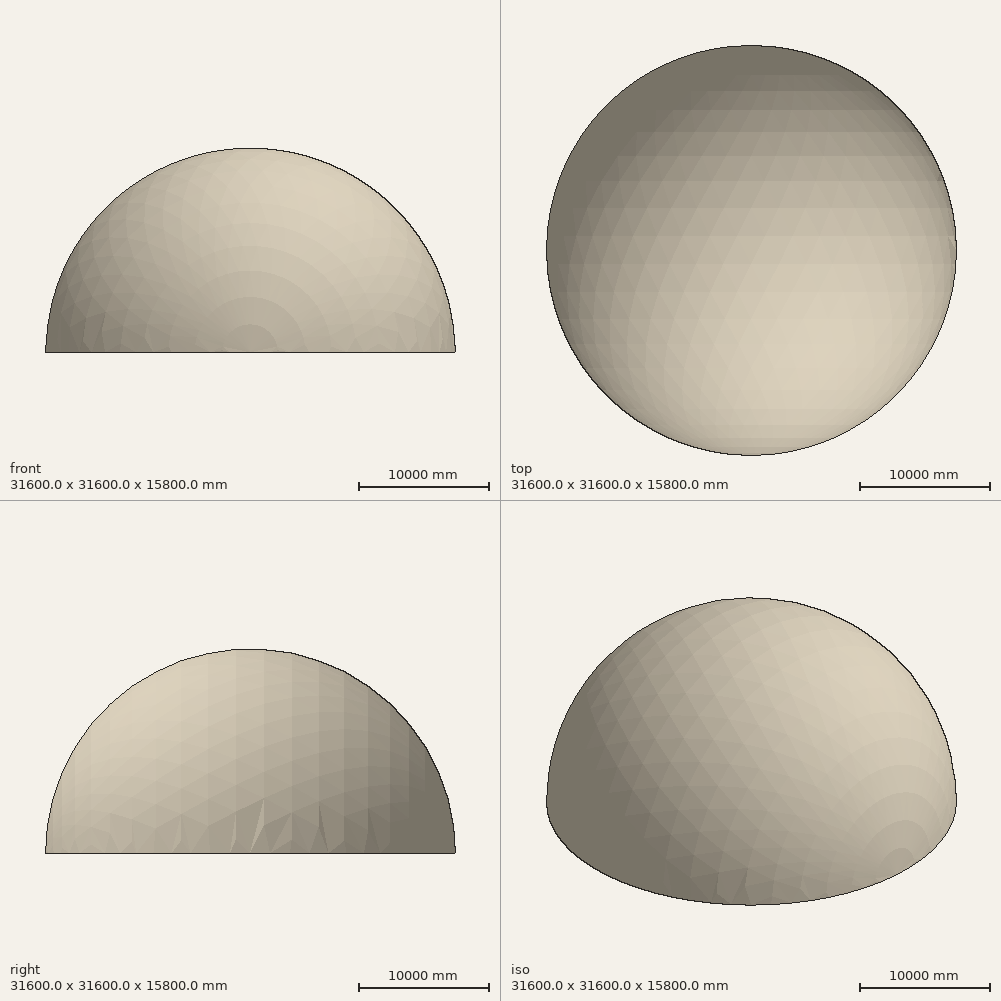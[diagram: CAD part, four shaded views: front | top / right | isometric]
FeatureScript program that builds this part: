
annotation { "Feature Type Name" : "Feature", "Feature Type Description" : "" }
export const myFeature = defineFeature(function(context is Context, id is Id, definition is map)
    precondition{}
    {
        {
            var Q0;
            Q0=qCreatedBy(makeId("Top.planeOp"),FACE);
            var sketch = newSketch(context, id + "F0", { "sketchPlane" : qUnion([Q0])});
            skArc(sketch, "E0", {"start": v(0, 14300) * mm, "mid": v(14300, 0) * mm, "end": v(0, -14300) * mm});
            skArc(sketch, "E1", {"start": v(0, 15800) * mm, "mid": v(15800, 0) * mm, "end": v(0, -15800) * mm});
            skLineSegment(sketch, "E2", {"start": v(0, 15800) * mm, "end": v(0, 14300) * mm});
            skLineSegment(sketch, "E3", {"start": v(0, -14300) * mm, "end": v(0, -15800) * mm});
            skSolve(sketch);
        }
        {
            var Q0;
            Q0 = qSketchRegion(id + "F0", true);
            var Q1;
            Q1=sQuery(id+"F0.wireOp",EDGE,"E2");
            revolve(context, id + "F1", {"surfaceOperationType" : NewSurfaceOperationType.NEW, "entities" : qUnion([Q0]), "axis" : qUnion([Q1]), "revolveType" : RevolveType.ONE_DIRECTION, "angle" : 180 * degree});
        }
    });
